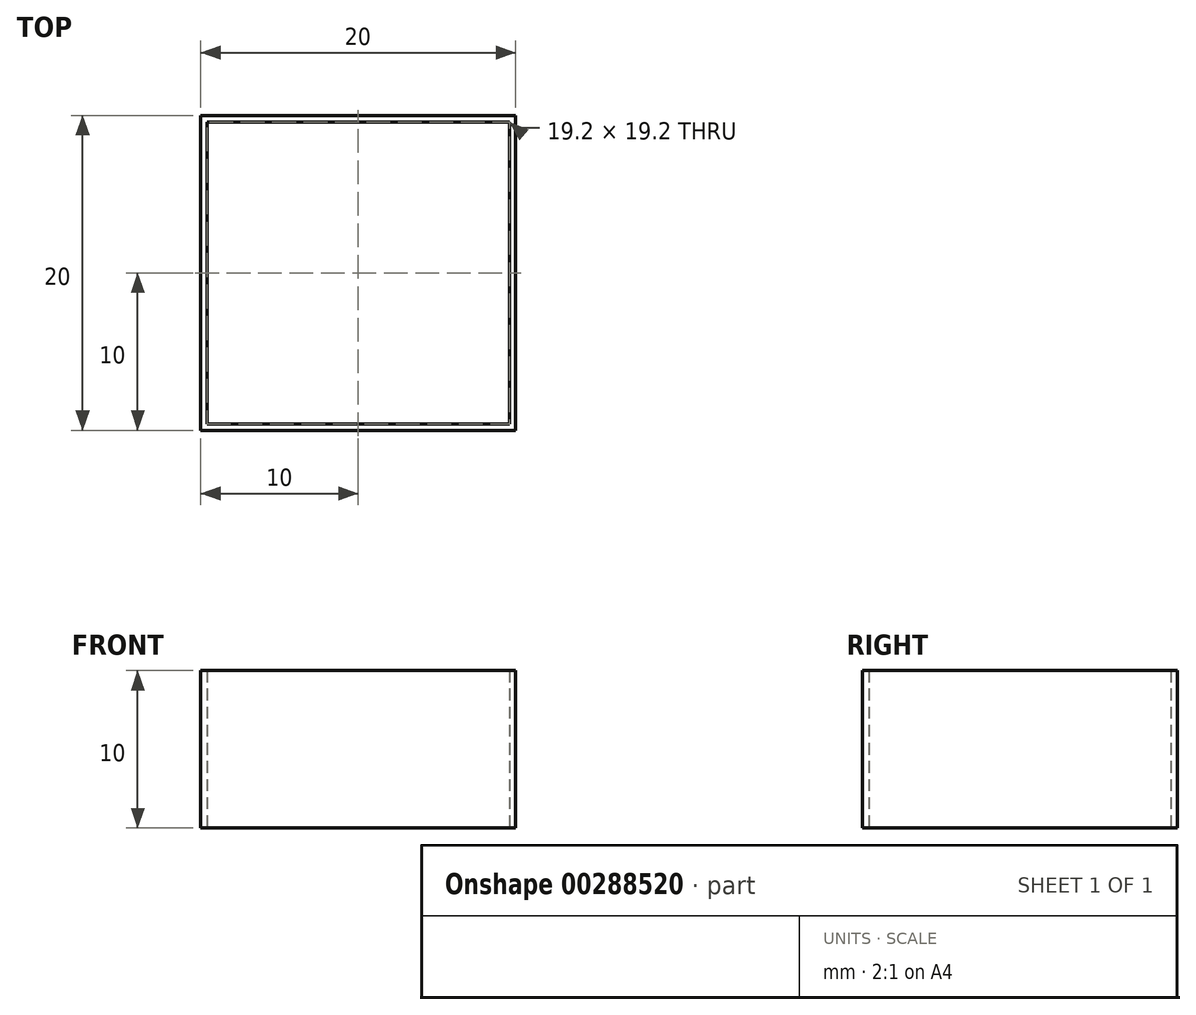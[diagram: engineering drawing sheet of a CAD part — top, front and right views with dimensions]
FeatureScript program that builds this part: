
annotation { "Feature Type Name" : "Feature", "Feature Type Description" : "" }
export const myFeature = defineFeature(function(context is Context, id is Id, definition is map)
    precondition{}
    {
        {
            var Q0;
            Q0=qCreatedBy(makeId("Top.planeOp"),FACE);
            var sketch = newSketch(context, id + "F0", { "sketchPlane" : qUnion([Q0])});
            skLineSegment(sketch, "E0.bottom", {"start": v(-10, -10) * mm, "end": v(10, -10) * mm});
            skLineSegment(sketch, "E0.top", {"start": v(-10, 10) * mm, "end": v(10, 10) * mm});
            skLineSegment(sketch, "E0.left", {"start": v(-10, -10) * mm, "end": v(-10, 10) * mm});
            skLineSegment(sketch, "E0.right", {"start": v(10, -10) * mm, "end": v(10, 10) * mm});
            skPoint(sketch, "E0.middle", {"position": v(0, 0) * mm});
            skLineSegment(sketch, "E1.bottom", {"start": v(-9.6, -9.6) * mm, "end": v(9.6, -9.6) * mm});
            skLineSegment(sketch, "E1.top", {"start": v(-9.6, 9.6) * mm, "end": v(9.6, 9.6) * mm});
            skLineSegment(sketch, "E1.left", {"start": v(-9.6, -9.6) * mm, "end": v(-9.6, 9.6) * mm});
            skLineSegment(sketch, "E1.right", {"start": v(9.6, -9.6) * mm, "end": v(9.6, 9.6) * mm});
            skSolve(sketch);
        }
        {
            var Q0;
            Q0 = qSketchRegion(id + "F0", true);
            extrude(context, id + "F1", {"entities" : qUnion([Q0]), "depth" : 10 * mm});
        }
    });
